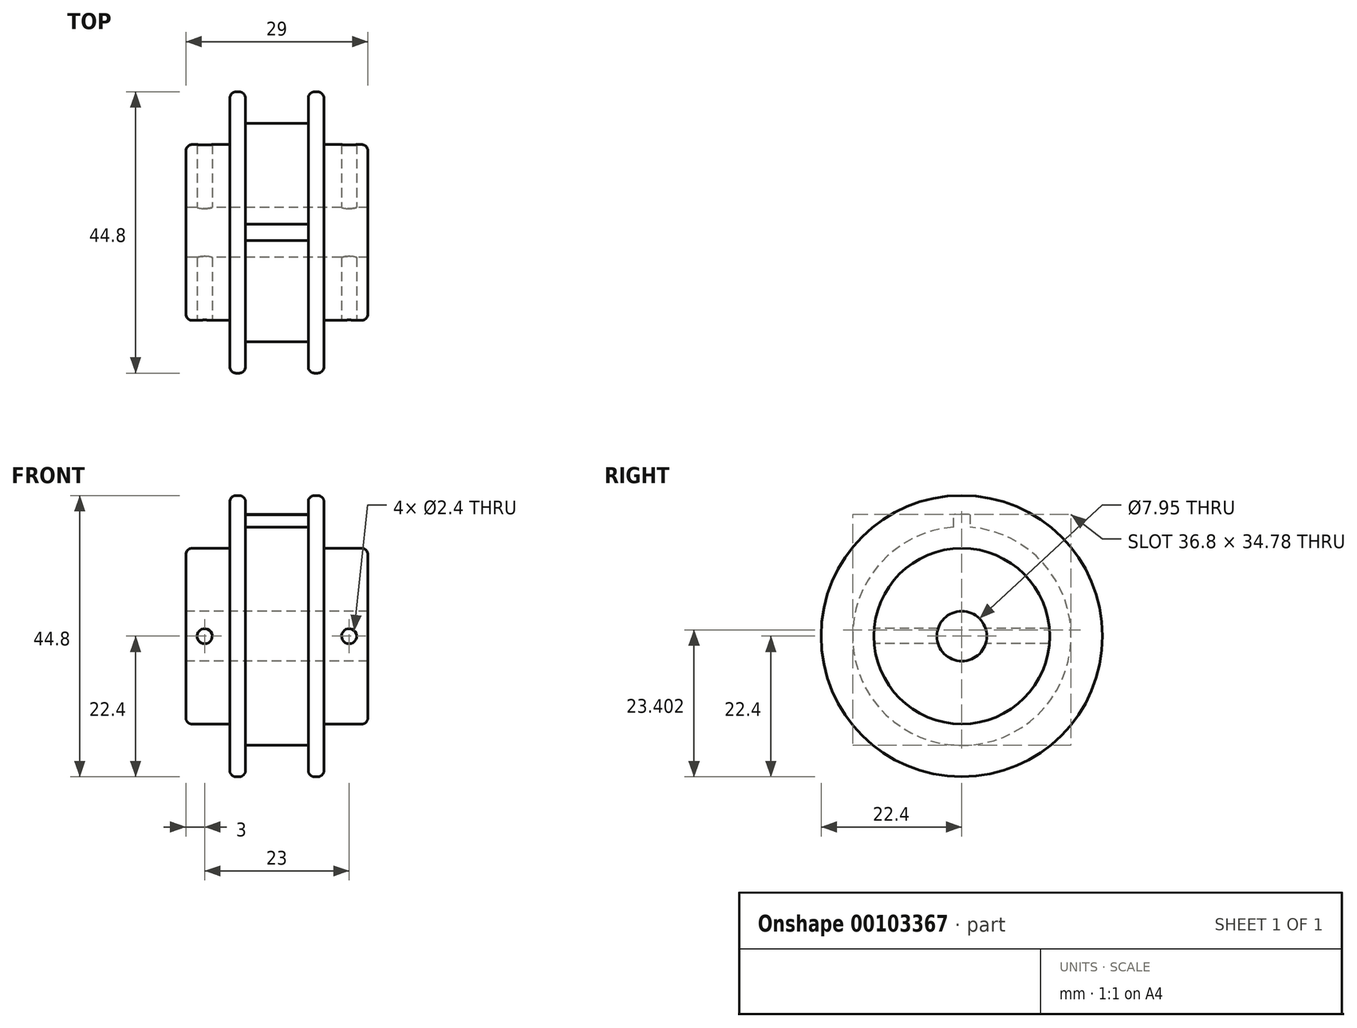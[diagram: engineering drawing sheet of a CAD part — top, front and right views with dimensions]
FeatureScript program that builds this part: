
annotation { "Feature Type Name" : "Feature", "Feature Type Description" : "" }
export const myFeature = defineFeature(function(context is Context, id is Id, definition is map)
    precondition{}
    {
        {
            var Q0;
            Q0=qCreatedBy(makeId("Right.planeOp"),FACE);
            var sketch = newSketch(context, id + "F0", { "sketchPlane" : qUnion([Q0])});
            skCircle(sketch, "E0", {"center": v(0, 0) * mm, "radius": 3.98 * mm});
            skCircle(sketch, "E1", {"center": v(0, 0) * mm, "radius": 14 * mm});
            skSolve(sketch);
        }
        {
            var Q0;
            Q0=makeQuery(id+"F0.imprint","IMPRINT",FACE,{"disambiguationData":[TD([[makeQuery(id+"F0.imprint","IMPRINT",EDGE,{"derivedFrom":sQuery(id+"F0.wireOp",EDGE,"E0")}),-1.0]])]});
            extrude(context, id + "F1", {"entities" : qUnion([Q0]), "endBound" : BoundingType.SYMMETRIC, "depth" : 29 * mm});
        }
        {
            var Q0;
            Q0=qCreatedBy(makeId("Right.planeOp"),FACE);
            var sketch = newSketch(context, id + "F2", { "sketchPlane" : qUnion([Q0])});
            skCircle(sketch, "E2", {"center": v(0, 0) * mm, "radius": 14 * mm});
            skCircle(sketch, "E3", {"center": v(0, 0) * mm, "radius": 17.4 * mm});
            skSolve(sketch);
        }
        {
            var Q0;
            Q0=makeQuery(id+"F2.imprint","IMPRINT",FACE,{"disambiguationData":[TD([[makeQuery(id+"F2.imprint","IMPRINT",EDGE,{"derivedFrom":sQuery(id+"F2.wireOp",EDGE,"E2")}),-1.0]])]});
            extrude(context, id + "F3", {"entities" : qUnion([Q0]), "operationType" : NewBodyOperationType.ADD, "endBound" : BoundingType.SYMMETRIC, "depth" : 15 * mm});
        }
        {
            var Q0;
            Q0=qCreatedBy(makeId("Front.planeOp"),FACE);
            var sketch = newSketch(context, id + "F4", { "sketchPlane" : qUnion([Q0])});
            skLineSegment(sketch, "E4", {"start": v(-27.37, 0) * mm, "end": v(29.66, 0) * mm});
            skLineSegment(sketch, "E5.bottom", {"start": v(-7.5, 22.4) * mm, "end": v(7.5, 22.4) * mm});
            skLineSegment(sketch, "E5.top", {"start": v(-7.5, 17.4) * mm, "end": v(7.5, 17.4) * mm});
            skLineSegment(sketch, "E5.left", {"start": v(-7.5, 22.4) * mm, "end": v(-7.5, 17.4) * mm});
            skLineSegment(sketch, "E5.right", {"start": v(7.5, 22.4) * mm, "end": v(7.5, 17.4) * mm});
            skLineSegment(sketch, "E6", {"start": v(-5, 22.4) * mm, "end": v(-5, 17.4) * mm});
            skLineSegment(sketch, "E7", {"start": v(5, 22.4) * mm, "end": v(5, 17.4) * mm});
            skSolve(sketch);
        }
        {
            var Q0;
            {var subQ0=sQuery(id+"F4.wireOp",EDGE,"E5.left");Q0=makeQuery(id+"F4.imprint","IMPRINT",FACE,{"disambiguationData":[TD([[makeQuery(id+"F4.imprint","IMPRINT",EDGE,{"derivedFrom":subQ0}),1.0]])]});}
            var Q1;
            {var subQ0=sQuery(id+"F4.wireOp",EDGE,"E5.right");Q1=makeQuery(id+"F4.imprint","IMPRINT",FACE,{"disambiguationData":[TD([[makeQuery(id+"F4.imprint","IMPRINT",EDGE,{"derivedFrom":subQ0}),-1.0]])]});}
            var Q2;
            Q2=sQuery(id+"F4.wireOp",EDGE,"E4");
            revolve(context, id + "F5", {"operationType" : NewBodyOperationType.ADD, "entities" : qUnion([Q0, Q1]), "axis" : qUnion([Q2]), "revolveType" : RevolveType.FULL});
        }
        {
            var Q0;
            Q0=qCreatedBy(makeId("Front.planeOp"),FACE);
            var sketch = newSketch(context, id + "F6", { "sketchPlane" : qUnion([Q0])});
            skCircle(sketch, "E8", {"center": v(-11.5, 0) * mm, "radius": 1.2 * mm});
            skCircle(sketch, "E9", {"center": v(11.5, 0) * mm, "radius": 1.2 * mm});
            skSolve(sketch);
        }
        {
            var Q0;
            Q0=makeQuery(id+"F6.imprint","IMPRINT",FACE,{"disambiguationData":[TD([[makeQuery(id+"F6.imprint","IMPRINT",EDGE,{"derivedFrom":sQuery(id+"F6.wireOp",EDGE,"E8")}),1.0]])]});
            var Q1;
            Q1=makeQuery(id+"F6.imprint","IMPRINT",FACE,{"disambiguationData":[TD([[makeQuery(id+"F6.imprint","IMPRINT",EDGE,{"derivedFrom":sQuery(id+"F6.wireOp",EDGE,"E9")}),1.0]])]});
            extrude(context, id + "F7", {"entities" : qUnion([Q0, Q1]), "operationType" : NewBodyOperationType.REMOVE, "endBound" : BoundingType.SYMMETRIC, "oppositeDirection" : true, "depth" : 30 * mm});
        }
        {
            var Q0;
            {var subQ0=sQuery(id+"F4.wireOp",EDGE,"E6");Q0=makeQuery(id+"FOtlNRIKVtqWGdL_1.boolean.opBoolean","MERGE",FACE,{"derivedFrom":[makeQuery(id+"F5.opRevolve","SWEPT_FACE",FACE,{"disambiguationData":[OSD([subQ0])]}),makeQuery(id+"FOtlNRIKVtqWGdL_1.opRevolve","SWEPT_FACE",FACE,{"disambiguationData":[OSD([subQ0])]})]});}
            var sketch = newSketch(context, id + "F8", { "sketchPlane" : qUnion([Q0])});
            skArc(sketch, "E10", {"start": v(-1.3, 17.35) * mm, "mid": v(0, -17.4) * mm, "end": v(1.3, 17.35) * mm, "construction": true});
            skArc(sketch, "E11", {"start": v(1.3, 17.35) * mm, "mid": v(0, 17.4) * mm, "end": v(-1.3, 17.35) * mm});
            skPoint(sketch, "E12.visualSharp", {"position": v(-1.3, 19.36) * mm});
            skPoint(sketch, "E13.visualSharp", {"position": v(1.3, 19.36) * mm});
            skArc(sketch, "E14", {"start": v(-0.97, 19.38) * mm, "mid": v(0, -19.4) * mm, "end": v(0.98, 19.38) * mm});
            skArc(sketch, "E15", {"start": v(0.98, 19.38) * mm, "mid": v(-0.29, 19.4) * mm, "end": v(-1.55, 19.34) * mm});
            skLineSegment(sketch, "E16", {"start": v(-1.3, 17.35) * mm, "end": v(-1.3, 19.36) * mm});
            skLineSegment(sketch, "E17", {"start": v(1.3, 19.36) * mm, "end": v(1.3, 17.35) * mm});
            skSolve(sketch);
        }
        {
            var Q0;
            {var subQ0=sQuery(id+"F8.wireOp",EDGE,"E15");var subQ3=makeQuery(id+"F8.imprint","IMPRINT",VERTEX,{"derivedFrom":subQ0});Q0=makeQuery(id+"F8.imprint","IMPRINT",FACE,{"disambiguationData":[TD([[makeQuery(id+"F8.imprint","IMPRINT",EDGE,{"disambiguationData":[TD([[subQ3,1.0]])],"derivedFrom":subQ0}),1.0]])]});}
            extrude(context, id + "F9", {"entities" : qUnion([Q0]), "operationType" : NewBodyOperationType.ADD, "depth" : 10 * mm});
        }
        {
            var Q0;
            Q0=makeQuery(id+"F5.opRevolve","SWEPT_EDGE",EDGE,{"disambiguationData":[OSD([sQuery(id+"F4.wireOp",EDGE,"E5.bottom"),sQuery(id+"F4.wireOp",EDGE,"E6")])]});
            var Q1;
            Q1=makeQuery(id+"F5.opRevolve","SWEPT_EDGE",EDGE,{"disambiguationData":[OSD([sQuery(id+"F4.wireOp",EDGE,"E5.bottom"),sQuery(id+"F4.wireOp",EDGE,"E7")])]});
            var Q2;
            Q2=makeQuery(id+"F1.opExtrude","CAP_EDGE",EDGE,{"disambiguationData":[OSD([sQuery(id+"F0.wireOp",EDGE,"E1")])],"isStart":true});
            var Q3;
            Q3=makeQuery(id+"F1.opExtrude","CAP_EDGE",EDGE,{"disambiguationData":[OSD([sQuery(id+"F0.wireOp",EDGE,"E1")])],"isStart":false});
            var Q4;
            Q4=makeQuery(id+"F5.opRevolve","SWEPT_EDGE",EDGE,{"disambiguationData":[OSD([sQuery(id+"F4.wireOp",EDGE,"E5.bottom"),sQuery(id+"F4.wireOp",EDGE,"E5.left")])]});
            var Q5;
            Q5=makeQuery(id+"F5.opRevolve","SWEPT_EDGE",EDGE,{"disambiguationData":[OSD([sQuery(id+"F4.wireOp",EDGE,"E5.bottom"),sQuery(id+"F4.wireOp",EDGE,"E5.right")])]});
            fillet(context, id + "F10", {"entities" : qUnion([Q0, Q1, Q2, Q3, Q4, Q5]), "radius" : 1 * mm, "tangentPropagation" : true, "allowEdgeOverflow" : false});
        }
    });
